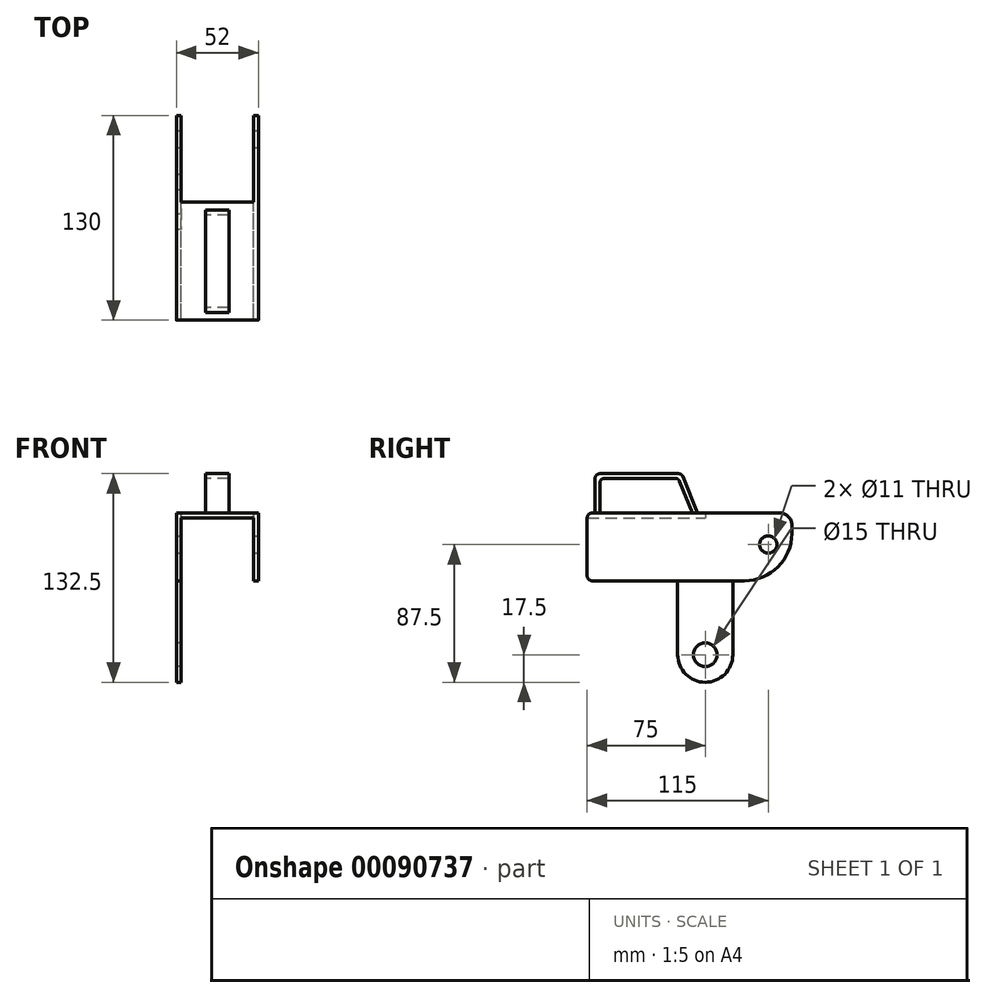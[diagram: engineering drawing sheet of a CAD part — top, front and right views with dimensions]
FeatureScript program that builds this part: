
annotation { "Feature Type Name" : "Feature", "Feature Type Description" : "" }
export const myFeature = defineFeature(function(context is Context, id is Id, definition is map)
    precondition{}
    {
        {
            var Q0;
            Q0=qCreatedBy(makeId("Front.planeOp"),FACE);
            var sketch = newSketch(context, id + "F0", { "sketchPlane" : qUnion([Q0])});
            skLineSegment(sketch, "E0.bottom", {"start": v(23, 20) * mm, "end": v(-23, 20) * mm});
            skLineSegment(sketch, "E0.left", {"start": v(23, 20) * mm, "end": v(23, -20) * mm});
            skLineSegment(sketch, "E0.right", {"start": v(-23, 20) * mm, "end": v(-23, -20) * mm});
            skPoint(sketch, "E0.middle", {"position": v(0, 0) * mm});
            skLineSegment(sketch, "E1.0", {"start": v(-26, 23) * mm, "end": v(-26, -20) * mm});
            skLineSegment(sketch, "E1.1", {"start": v(26, 23) * mm, "end": v(-26, 23) * mm});
            skLineSegment(sketch, "E1.2", {"start": v(26, 23) * mm, "end": v(26, -20) * mm});
            skLineSegment(sketch, "E2", {"start": v(-26, -20) * mm, "end": v(-23, -20) * mm});
            skLineSegment(sketch, "E3", {"start": v(23, -20) * mm, "end": v(26, -20) * mm});
            skSolve(sketch);
        }
        {
            var Q0;
            Q0 = qSketchRegion(id + "F0", true);
            extrude(context, id + "F1", {"entities" : qUnion([Q0]), "endBound" : BoundingType.SYMMETRIC, "depth" : 130 * mm});
        }
        {
            var Q0;
            Q0=makeQuery(id+"F1.opExtrude","SWEPT_FACE",FACE,{"disambiguationData":[OSD([sQuery(id+"F0.wireOp",EDGE,"E1.2")])]});
            var sketch = newSketch(context, id + "F2", { "sketchPlane" : qUnion([Q0])});
            skCircle(sketch, "E4", {"center": v(50, 3) * mm, "radius": 5.5 * mm});
            skCircle(sketch, "E5", {"center": v(35, 10) * mm, "radius": 30 * mm});
            skCircle(sketch, "E6", {"center": v(57.5, 15.5) * mm, "radius": 7.5 * mm});
            skSolve(sketch);
        }
        {
            var Q0;
            {var subQ0=sQuery(id+"F2.wireOp",EDGE,"pmkFaM8B-aZ52-WYXZ-YjHk-OsGlzKAUHM6I");var subQ1=sQuery(id+"F2.wireOp",EDGE,"E4");var subQ2=makeQuery(id+"F2.imprint","INTERSECT",VERTEX,{"disambiguationData":[OD(0.0)],"derivedFrom":[subQ1,subQ0]});Q0=makeQuery(id+"F2.imprint","IMPRINT",FACE,{"disambiguationData":[TD([[makeQuery(id+"F2.imprint","IMPRINT",EDGE,{"disambiguationData":[TD([[subQ2,1.0]])],"derivedFrom":subQ1}),1.0]])]});}
            var Q1;
            {var subQ0=sQuery(id+"F2.wireOp",EDGE,"pmkFaM8B-aZ52-WYXZ-YjHk-OsGlzKAUHM6I");var subQ1=sQuery(id+"F2.wireOp",EDGE,"E4");var subQ2=makeQuery(id+"F2.imprint","INTERSECT",VERTEX,{"disambiguationData":[OD(0.0)],"derivedFrom":[subQ1,subQ0]});Q1=makeQuery(id+"F2.imprint","IMPRINT",FACE,{"disambiguationData":[TD([[makeQuery(id+"F2.imprint","IMPRINT",EDGE,{"disambiguationData":[TD([[subQ2,-1.0]])],"derivedFrom":subQ1}),1.0]])]});}
            var Q2;
            {var subQ0=sQuery(id+"F2.wireOp",EDGE,"MWgSsply-w0km-exgx-j7se-lkpM5lSmd5LQ");Q2=makeQuery(id+"F2.imprint","IMPRINT",FACE,{"disambiguationData":[TD([[makeQuery(id+"F2.imprint","IMPRINT",EDGE,{"derivedFrom":subQ0}),-1.0]])]});}
            var Q3;
            {var subQ0=sQuery(id+"F2.wireOp",EDGE,"pmkFaM8B-aZ52-WYXZ-YjHk-OsGlzKAUHM6I");var subQ1=sQuery(id+"F0.wireOp",EDGE,"E1.2");var subQ4=makeQuery(id+"F1.opExtrude","CAP_EDGE",EDGE,{"disambiguationData":[OSD([subQ1])],"isStart":true});var subQ5=makeQuery(id+"F2.imprint","INTERSECT",VERTEX,{"derivedFrom":[subQ4,subQ0]});Q3=makeQuery(id+"F2.imprint","IMPRINT",FACE,{"disambiguationData":[TD([[makeQuery(id+"F2.imprint","IMPRINT",EDGE,{"disambiguationData":[TD([[subQ5,-1.0]])],"derivedFrom":subQ0}),-1.0]])]});}
            var Q4;
            {var subQ0=sQuery(id+"F2.wireOp",EDGE,"Uxi5OEZw-8Aqg-K1lU-Y56c-l56xz1c9junp");Q4=makeQuery(id+"F2.imprint","IMPRINT",FACE,{"disambiguationData":[TD([[makeQuery(id+"F2.imprint","IMPRINT",EDGE,{"derivedFrom":subQ0}),1.0]])]});}
            var Q5;
            Q5=makeQuery(id+"F2.imprint","IMPRINT",FACE,{"disambiguationData":[TD([[makeQuery(id+"F2.imprint","IMPRINT",EDGE,{"derivedFrom":sQuery(id+"F2.wireOp",EDGE,"E4")}),1.0]])]});
            var Q6;
            {var subQ0=sQuery(id+"F2.wireOp",EDGE,"aiEnJqgv-5xcx-vpRv-OaVa-ciVkzgUmsryD");Q6=makeQuery(id+"F2.imprint","IMPRINT",FACE,{"disambiguationData":[TD([[makeQuery(id+"F2.imprint","IMPRINT",EDGE,{"derivedFrom":subQ0}),1.0]])]});}
            var Q7;
            {var subQ0=sQuery(id+"F2.wireOp",EDGE,"E5");var subQ1=sQuery(id+"F0.wireOp",EDGE,"E1.2");var subQ2=makeQuery(id+"F1.opExtrude","CAP_EDGE",EDGE,{"disambiguationData":[OSD([subQ1])],"isStart":true});var subQ3=makeQuery(id+"F2.imprint","INTERSECT",VERTEX,{"derivedFrom":[subQ2,subQ0]});Q7=makeQuery(id+"F2.imprint","IMPRINT",FACE,{"disambiguationData":[TD([[makeQuery(id+"F2.imprint","IMPRINT",EDGE,{"disambiguationData":[TD([[subQ3,1.0]])],"derivedFrom":subQ0}),-1.0]])]});}
            var Q8;
            {var subQ0=sQuery(id+"F2.wireOp",EDGE,"aiEnJqgv-5xcx-vpRv-OaVa-ciVkzgUmsryD");var subQ1=sQuery(id+"F0.wireOp",EDGE,"E1.2");var subQ2=makeQuery(id+"F1.opExtrude","CAP_EDGE",EDGE,{"disambiguationData":[OSD([subQ1])],"isStart":true});var subQ3=makeQuery(id+"F2.imprint","INTERSECT",VERTEX,{"derivedFrom":[subQ2,subQ0]});Q8=makeQuery(id+"F2.imprint","IMPRINT",FACE,{"disambiguationData":[TD([[makeQuery(id+"F2.imprint","IMPRINT",EDGE,{"disambiguationData":[TD([[subQ3,1.0]])],"derivedFrom":subQ0}),1.0]])]});}
            var Q9;
            {var subQ0=sQuery(id+"F2.wireOp",EDGE,"E6");var subQ1=sQuery(id+"F2.wireOp",EDGE,"E5");var subQ2=makeQuery(id+"F2.imprint","INTERSECT",VERTEX,{"disambiguationData":[OD(1.0)],"derivedFrom":[subQ1,subQ0]});Q9=makeQuery(id+"F2.imprint","IMPRINT",FACE,{"disambiguationData":[TD([[makeQuery(id+"F2.imprint","IMPRINT",EDGE,{"disambiguationData":[TD([[subQ2,1.0]])],"derivedFrom":subQ0}),-1.0]])]});}
            var Q10;
            {var subQ0=sQuery(id+"F2.wireOp",EDGE,"E6");var subQ1=sQuery(id+"F2.wireOp",EDGE,"E5");var subQ2=makeQuery(id+"F2.imprint","INTERSECT",VERTEX,{"disambiguationData":[OD(1.0)],"derivedFrom":[subQ1,subQ0]});Q10=makeQuery(id+"F2.imprint","IMPRINT",FACE,{"disambiguationData":[TD([[makeQuery(id+"F2.imprint","IMPRINT",EDGE,{"disambiguationData":[TD([[subQ2,-1.0]])],"derivedFrom":subQ1}),1.0]])]});}
            extrude(context, id + "F3", {"entities" : qUnion([Q0, Q1, Q2, Q3, Q4, Q5, Q6, Q7, Q8, Q9, Q10]), "operationType" : NewBodyOperationType.REMOVE, "endBound" : BoundingType.THROUGH_ALL, "oppositeDirection" : true, "depth" : 25 * mm});
        }
        {
            var Q0;
            Q0=makeQuery(id+"F1.opExtrude","SWEPT_FACE",FACE,{"disambiguationData":[OSD([sQuery(id+"F0.wireOp",EDGE,"E0.bottom")])]});
            var sketch = newSketch(context, id + "F4", { "sketchPlane" : qUnion([Q0])});
            skLineSegment(sketch, "E7.bottom", {"start": v(23, -10) * mm, "end": v(-23, -10) * mm});
            skLineSegment(sketch, "E7.top", {"start": v(23, -65) * mm, "end": v(-23, -65) * mm});
            skLineSegment(sketch, "E7.left", {"start": v(23, -10) * mm, "end": v(23, -65) * mm});
            skLineSegment(sketch, "E7.right", {"start": v(-23, -10) * mm, "end": v(-23, -65) * mm});
            skSolve(sketch);
        }
        {
            var Q0;
            Q0 = qSketchRegion(id + "F4", true);
            extrude(context, id + "F5", {"entities" : qUnion([Q0]), "operationType" : NewBodyOperationType.REMOVE, "oppositeDirection" : true, "depth" : 25 * mm});
        }
        {
            var Q0;
            Q0=qCreatedBy(makeId("Right.planeOp"),FACE);
            var sketch = newSketch(context, id + "F6", { "sketchPlane" : qUnion([Q0])});
            skLineSegment(sketch, "E8", {"start": v(-60, 23) * mm, "end": v(-60, 48) * mm});
            skLineSegment(sketch, "E9", {"start": v(-60, 48) * mm, "end": v(-5, 48) * mm});
            skLineSegment(sketch, "E10", {"start": v(5, 23) * mm, "end": v(-5, 48) * mm});
            skLineSegment(sketch, "E11.0", {"start": v(1.77, 23) * mm, "end": v(-7.03, 45) * mm});
            skLineSegment(sketch, "E11.1", {"start": v(-57, 45) * mm, "end": v(-7.03, 45) * mm});
            skLineSegment(sketch, "E11.2", {"start": v(-57, 23) * mm, "end": v(-57, 45) * mm});
            skLineSegment(sketch, "E12", {"start": v(1.77, 23) * mm, "end": v(5, 23) * mm});
            skLineSegment(sketch, "E13", {"start": v(-57, 23) * mm, "end": v(-60, 23) * mm});
            skSolve(sketch);
        }
        {
            var Q0;
            Q0 = qSketchRegion(id + "F6", true);
            extrude(context, id + "F7", {"entities" : qUnion([Q0]), "operationType" : NewBodyOperationType.ADD, "endBound" : BoundingType.SYMMETRIC, "depth" : 15 * mm});
        }
        {
            var Q0;
            Q0=makeQuery(id+"F1.opExtrude","SWEPT_FACE",FACE,{"disambiguationData":[OSD([sQuery(id+"F0.wireOp",EDGE,"E1.0")])]});
            var sketch = newSketch(context, id + "F8", { "sketchPlane" : qUnion([Q0])});
            skLineSegment(sketch, "E14.bottom", {"start": v(-27.5, -20) * mm, "end": v(7.5, -20) * mm});
            skLineSegment(sketch, "E14.left", {"start": v(-27.5, -20) * mm, "end": v(-27.5, -67) * mm});
            skLineSegment(sketch, "E14.right", {"start": v(7.5, -20) * mm, "end": v(7.5, -67) * mm});
            skCircle(sketch, "E15", {"center": v(-10, -67) * mm, "radius": 7.5 * mm});
            skCircle(sketch, "E16", {"center": v(-10, -67) * mm, "radius": 17.5 * mm});
            skSolve(sketch);
        }
        {
            var Q0;
            Q0 = qSketchRegion(id + "F8", true);
            extrude(context, id + "F9", {"entities" : qUnion([Q0]), "operationType" : NewBodyOperationType.ADD, "oppositeDirection" : true, "depth" : 3 * mm});
        }
        {
            var Q0;
            Q0=makeQuery(id+"F1.opExtrude","CAP_EDGE",EDGE,{"disambiguationData":[OSD([sQuery(id+"F0.wireOp",EDGE,"E3")])],"isStart":false});
            var Q1;
            Q1=makeQuery(id+"F1.opExtrude","CAP_EDGE",EDGE,{"disambiguationData":[OSD([sQuery(id+"F0.wireOp",EDGE,"E2")])],"isStart":false});
            var Q2;
            Q2=makeQuery(id+"F7.opExtrude","SWEPT_EDGE",EDGE,{"disambiguationData":[OSD([sQuery(id+"F6.wireOp",EDGE,"E8"),sQuery(id+"F6.wireOp",EDGE,"E9")])]});
            var Q3;
            Q3=makeQuery(id+"F7.opExtrude","SWEPT_EDGE",EDGE,{"disambiguationData":[OSD([sQuery(id+"F6.wireOp",EDGE,"E11.1"),sQuery(id+"F6.wireOp",EDGE,"E11.2")])]});
            var Q4;
            Q4=makeQuery(id+"F7.opExtrude","SWEPT_EDGE",EDGE,{"disambiguationData":[OSD([sQuery(id+"F6.wireOp",EDGE,"E11.0"),sQuery(id+"F6.wireOp",EDGE,"E11.1")])]});
            var Q5;
            Q5=makeQuery(id+"F7.opExtrude","SWEPT_EDGE",EDGE,{"disambiguationData":[OSD([sQuery(id+"F6.wireOp",EDGE,"E9"),sQuery(id+"F6.wireOp",EDGE,"E10")])]});
            var Q6;
            Q6=makeQuery(id+"F1.opExtrude","CAP_EDGE",EDGE,{"disambiguationData":[OSD([sQuery(id+"F0.wireOp",EDGE,"E1.1")])],"isStart":false});
            fillet(context, id + "F10", {"entities" : qUnion([Q0, Q1, Q2, Q3, Q4, Q5, Q6]), "radius" : 3 * mm, "tangentPropagation" : true, "allowEdgeOverflow" : false});
        }
    });
